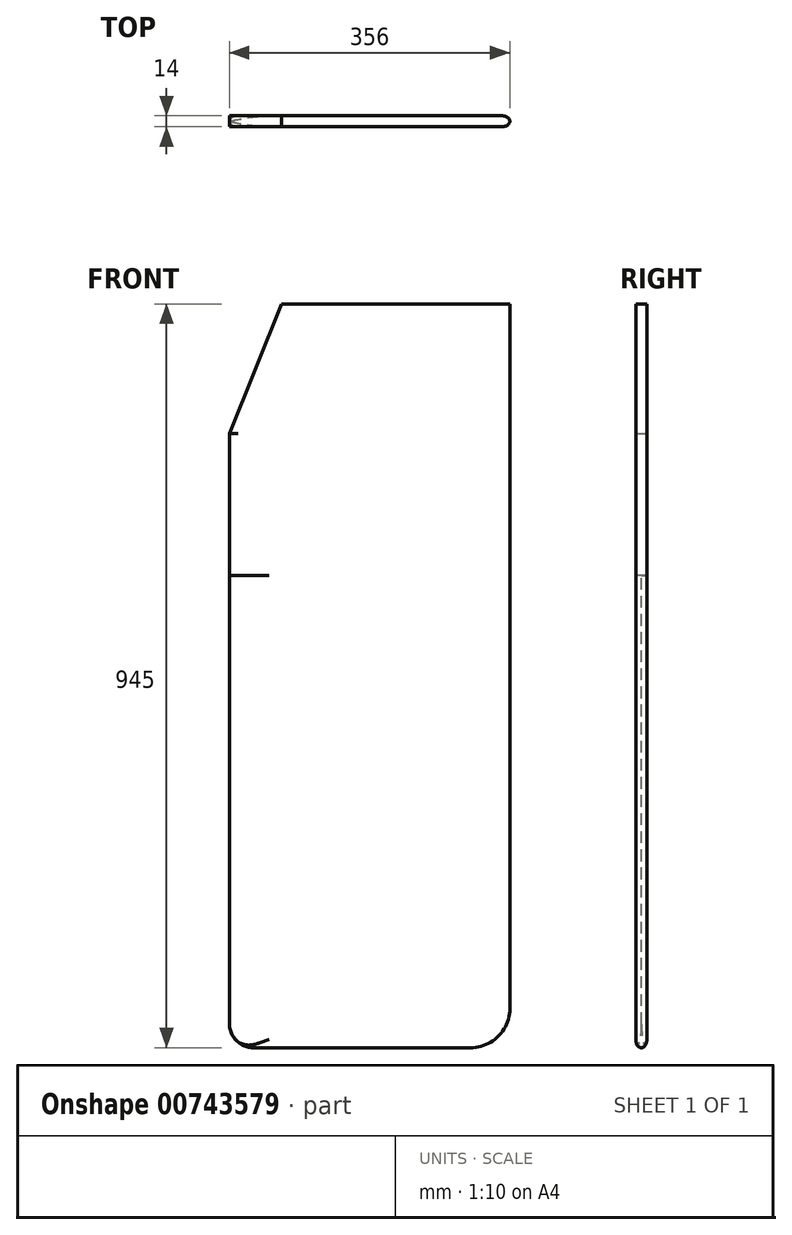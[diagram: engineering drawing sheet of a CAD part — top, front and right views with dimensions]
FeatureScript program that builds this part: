
annotation { "Feature Type Name" : "Feature", "Feature Type Description" : "" }
export const myFeature = defineFeature(function(context is Context, id is Id, definition is map)
    precondition{}
    {
        {
            var Q0;
            Q0=qCreatedBy(makeId("Top.planeOp"),FACE);
            cPlane(context, id + "F0", {"entities" : qUnion([Q0]), "cplaneType" : CPlaneType.OFFSET, "offset" : 345 * mm, "oppositeDirection" : true, "width" : 150 * mm, "height" : 150 * mm});
        }
        {
            var Q0;
            Q0=qCreatedBy(makeId("Front.planeOp"),FACE);
            var sketch = newSketch(context, id + "F1", { "sketchPlane" : qUnion([Q0])});
            skLineSegment(sketch, "E0.bottom", {"start": v(0, 0) * mm, "end": v(-290, 0) * mm});
            skLineSegment(sketch, "E0.top", {"start": v(-50, -945) * mm, "end": v(-326, -945) * mm});
            skLineSegment(sketch, "E0.left", {"start": v(0, 0) * mm, "end": v(0, -895) * mm});
            skLineSegment(sketch, "E0.right", {"start": v(-356, -165) * mm, "end": v(-356, -915) * mm});
            skLineSegment(sketch, "E1", {"start": v(-290, 0) * mm, "end": v(-356, -165) * mm});
            skPoint(sketch, "E2.visualSharp", {"position": v(-356, -945) * mm});
            skArc(sketch, "E2.filletArc", {"start": v(-356, -915) * mm, "mid": v(-347.21, -936.21) * mm, "end": v(-326, -945) * mm});
            skPoint(sketch, "E3.visualSharp", {"position": v(0, -945) * mm});
            skArc(sketch, "E3.filletArc", {"start": v(-50, -945) * mm, "mid": v(-14.64, -930.36) * mm, "end": v(0, -895) * mm});
            skLineSegment(sketch, "E4", {"start": v(-306, -40) * mm, "end": v(-306, -945) * mm, "construction": true});
            skLineSegment(sketch, "E5", {"start": v(-50, 0) * mm, "end": v(-50, -945) * mm, "construction": true});
            skSolve(sketch);
        }
        {
            var Q0;
            Q0=makeQuery(id+"F1.imprint","IMPRINT",FACE,{"disambiguationData":[TD([[makeQuery(id+"F1.imprint","IMPRINT",EDGE,{"derivedFrom":sQuery(id+"F1.wireOp",EDGE,"E0.bottom")}),1.0]])]});
            extrude(context, id + "F2", {"entities" : qUnion([Q0]), "endBound" : BoundingType.SYMMETRIC, "depth" : 14 * mm, "offsetDistance" : 25 * mm});
        }
        {
            var Q0;
            Q0=qCreatedBy(makeId("Top.planeOp"),FACE);
            var sketch = newSketch(context, id + "F3", { "sketchPlane" : qUnion([Q0])});
            skEllipticalArc(sketch, "E6", {});
            skLineSegment(sketch, "E7", {"start": v(-10.5, -11.42) * mm, "end": v(-10.5, 9.9) * mm, "construction": true});
            skLineSegment(sketch, "E8", {"start": v(-10.5, -7) * mm, "end": v(-10.5, -11) * mm});
            skLineSegment(sketch, "E9", {"start": v(-10.5, -11) * mm, "end": v(2.96, -11) * mm});
            skLineSegment(sketch, "E10", {"start": v(2.96, -11) * mm, "end": v(2.96, 9.65) * mm});
            skLineSegment(sketch, "E11", {"start": v(2.96, 9.65) * mm, "end": v(-10.5, 9.65) * mm});
            skLineSegment(sketch, "E12", {"start": v(-10.5, 9.65) * mm, "end": v(-10.5, 7) * mm});
            const initialGuessF3  = {"E6": [-0.0105, 0, -1, 0, 0.0105, 0.007, 1.5707963267948966, 4.71238898038469]};
            skSetInitialGuess(sketch, initialGuessF3);
            skSolve(sketch);
        }
        {
            var Q0;
            Q0=qCreatedBy(makeId("Top.planeOp"),FACE);
            var sketch = newSketch(context, id + "F4", { "sketchPlane" : qUnion([Q0])});
            skLineSegment(sketch, "E13.0", {"start": v(-356, 7) * mm, "end": v(-326, 7) * mm, "construction": true});
            skLineSegment(sketch, "E14.0", {"start": v(-356, 0) * mm, "end": v(-326, 0) * mm, "construction": true});
            skLineSegment(sketch, "E15.MirrorCS", {"start": v(-352.42, -0.97) * mm, "end": v(-348.85, -1.63) * mm, "construction": true});
            skLineSegment(sketch, "E16.MirrorCS", {"start": v(-356, 0.17) * mm, "end": v(-352.43, 1) * mm, "construction": true});
            skLineSegment(sketch, "E17.MirrorCS", {"start": v(-352.43, 1) * mm, "end": v(-348.86, 1.67) * mm, "construction": true});
            skLineSegment(sketch, "E18.MirrorCS", {"start": v(-327.26, -5.33) * mm, "end": v(-320.11, -6.17) * mm, "construction": true});
            skLineSegment(sketch, "E19.MirrorCS", {"start": v(-334.57, -4.3) * mm, "end": v(-327.43, -5.3) * mm, "construction": true});
            skLineSegment(sketch, "E20.MirrorCS", {"start": v(-313.14, 6.83) * mm, "end": v(-306, 7) * mm, "construction": true});
            skLineSegment(sketch, "E21.MirrorCS", {"start": v(-320.29, 6.17) * mm, "end": v(-313.14, 6.83) * mm, "construction": true});
            skLineSegment(sketch, "E22.MirrorCS", {"start": v(-327.43, 5.33) * mm, "end": v(-320.29, 6.17) * mm, "construction": true});
            skLineSegment(sketch, "E23.MirrorCS", {"start": v(-334.57, 4.33) * mm, "end": v(-327.43, 5.33) * mm, "construction": true});
            skLineSegment(sketch, "E24.MirrorCS", {"start": v(-341.71, 3) * mm, "end": v(-334.57, 4.33) * mm, "construction": true});
            skLineSegment(sketch, "E25.MirrorCS", {"start": v(-348.86, 1.67) * mm, "end": v(-341.71, 3) * mm, "construction": true});
            skLineSegment(sketch, "E26.MirrorCS", {"start": v(-312.97, -6.83) * mm, "end": v(-306.05, -7) * mm, "construction": true});
            skLineSegment(sketch, "E27.MirrorCS", {"start": v(-306, 7) * mm, "end": v(-356, 7) * mm, "construction": true});
            skLineSegment(sketch, "E28.MirrorCS", {"start": v(-341.7, -2.97) * mm, "end": v(-334.4, -4.33) * mm, "construction": true});
            skLineSegment(sketch, "E29.MirrorCS", {"start": v(-348.68, -1.67) * mm, "end": v(-341.54, -3) * mm, "construction": true});
            skLineSegment(sketch, "E30.MirrorCS", {"start": v(-355.83, -0.17) * mm, "end": v(-352.26, -1) * mm, "construction": true});
            skLineSegment(sketch, "E31.MirrorCS", {"start": v(-356, 7) * mm, "end": v(-356, -7) * mm, "construction": true});
            skLineSegment(sketch, "E32.MirrorCS", {"start": v(-320.29, -6.15) * mm, "end": v(-313.14, -6.82) * mm, "construction": true});
            skLineSegment(sketch, "E33", {"start": v(-356, 7) * mm, "end": v(0, 7) * mm});
            skLineSegment(sketch, "E34.MirrorCS", {"start": v(-43.03, -6.83) * mm, "end": v(-49.95, -7) * mm, "construction": true});
            skLineSegment(sketch, "E35.0", {"start": v(-306, 7) * mm, "end": v(-306, -7) * mm, "construction": true});
            skFitSpline(sketch, "E36", {"points": [v(-356, 0) * mm, v(-355.83, -0.17) * mm, v(-352.42, -0.97) * mm, v(-341.54, -3) * mm, v(-331.25, -3.91) * mm], "startDerivative": vector(1.96, -3) * mm, "endDerivative": vector(27.6, -1.63) * mm});
            skSolve(sketch);
        }
        {
            var Q0;
            Q0=qCreatedBy(id+"F0.planeOp",FACE);
            var sketch = newSketch(context, id + "F5", { "sketchPlane" : qUnion([Q0])});
            skFitSpline(sketch, "E37", {"points": [v(-356, 0) * mm, v(-355.82, -0.17) * mm, v(-352.22, -1) * mm, v(-344.2, -2.51) * mm, v(-334.25, -4.34) * mm, v(-327.32, -5.3) * mm, v(-320.11, -6.16) * mm, v(-312.8, -6.83) * mm, v(-306, -7) * mm], "startDerivative": vector(0.04, -5.2) * mm, "endDerivative": vector(51.3, -0.2) * mm});
            skLineSegment(sketch, "E38", {"start": v(-306, -7) * mm, "end": v(-306, -8.18) * mm});
            skLineSegment(sketch, "E39", {"start": v(-306, -8.18) * mm, "end": v(-357.4, -8.18) * mm});
            skLineSegment(sketch, "E40.0", {"start": v(-356, -7) * mm, "end": v(-356, 7) * mm, "construction": true});
            skLineSegment(sketch, "E41", {"start": v(-356, 0) * mm, "end": v(-357.14, 0) * mm, "construction": true});
            skFitSpline(sketch, "E42.MirrorCS", {"points": [v(-356, 0) * mm, v(-355.82, 0.17) * mm, v(-352.22, 1) * mm, v(-344.2, 2.51) * mm, v(-334.25, 4.34) * mm, v(-327.32, 5.3) * mm, v(-320.11, 6.16) * mm, v(-312.8, 6.83) * mm, v(-306, 7) * mm], "startDerivative": vector(0.04, 5.2) * mm, "endDerivative": vector(51.3, 0.2) * mm});
            skLineSegment(sketch, "E43.MirrorCS", {"start": v(-306, 7) * mm, "end": v(-306, 8.18) * mm});
            skLineSegment(sketch, "E44.MirrorCS", {"start": v(-306, 8.18) * mm, "end": v(-357.4, 8.18) * mm});
            skLineSegment(sketch, "E45", {"start": v(-357.4, 8.18) * mm, "end": v(-357.4, -8.18) * mm});
            skSolve(sketch);
        }
        {
            var Q0;
            Q0=qCreatedBy(makeId("Front.planeOp"),FACE);
            var sketch = newSketch(context, id + "F6", { "sketchPlane" : qUnion([Q0])});
            skLineSegment(sketch, "E46.0", {"start": v(0, 0) * mm, "end": v(0, -895) * mm});
            skArc(sketch, "E46.1", {"start": v(-50, -945) * mm, "mid": v(-14.64, -930.36) * mm, "end": v(0, -895) * mm});
            skLineSegment(sketch, "E47.0", {"start": v(-50, -945) * mm, "end": v(-326, -945) * mm});
            skArc(sketch, "E48.0", {"start": v(-356, -915) * mm, "mid": v(-347.21, -936.21) * mm, "end": v(-326, -945) * mm});
            skLineSegment(sketch, "E49.0", {"start": v(-356, -165) * mm, "end": v(-356, -915) * mm});
            skSolve(sketch);
        }
        {
            var Q0;
            Q0=makeQuery(id+"F3.imprint","IMPRINT",FACE,{"disambiguationData":[TD([[makeQuery(id+"F3.imprint","IMPRINT",EDGE,{"derivedFrom":sQuery(id+"F3.wireOp",EDGE,"E6")}),-1.0]])]});
            var Q1;
            Q1 = qConstructionFilter(qBodyType(qCreatedBy(id + "F6" ,EDGE), BodyType.WIRE), ConstructionObject.NO);
            sweep(context, id + "F7", {"operationType" : NewBodyOperationType.REMOVE, "profiles" : qUnion([Q0]), "path" : qUnion([Q1])});
        }
        {
            var Q0;
            Q0=makeQuery(id+"F5.imprint","IMPRINT",FACE,{"disambiguationData":[TD([[makeQuery(id+"F5.imprint","IMPRINT",EDGE,{"derivedFrom":sQuery(id+"F5.wireOp",EDGE,"E37")}),-1.0]])]});
            extrude(context, id + "F8", {"entities" : qUnion([Q0]), "operationType" : NewBodyOperationType.REMOVE, "oppositeDirection" : true, "depth" : 975 * mm, "offsetDistance" : 25 * mm});
        }
    });
